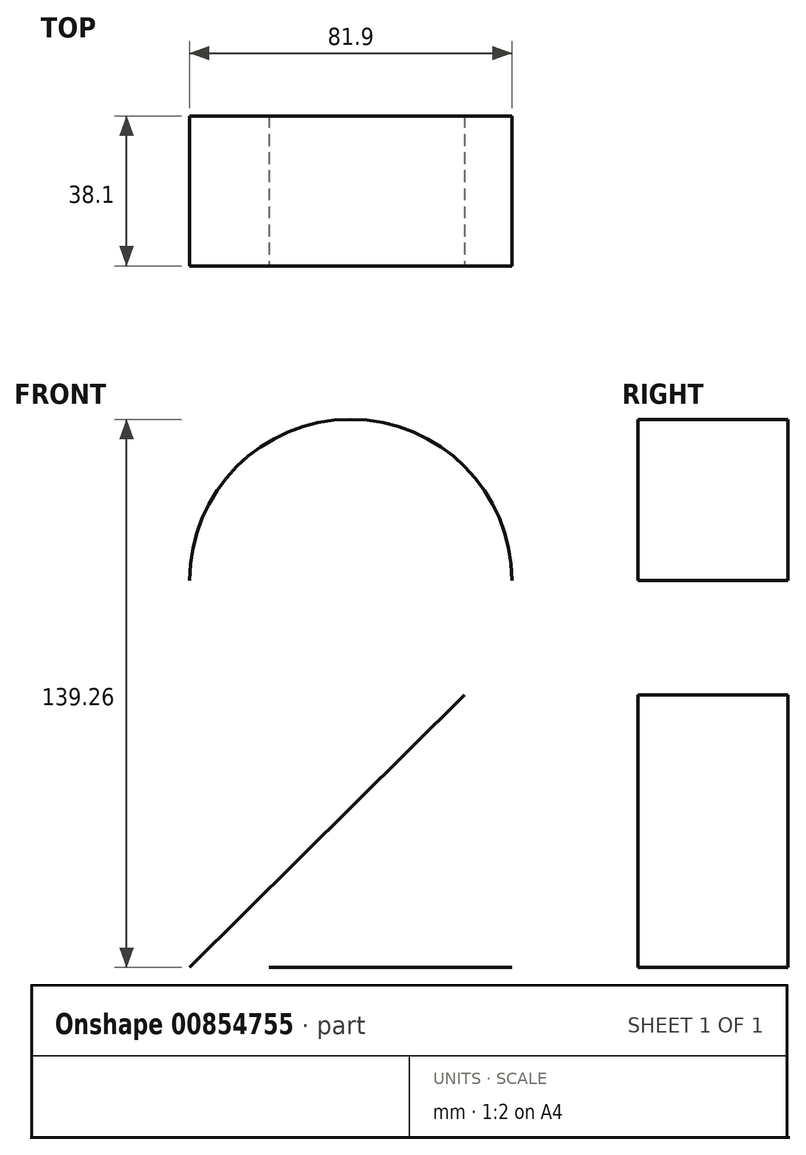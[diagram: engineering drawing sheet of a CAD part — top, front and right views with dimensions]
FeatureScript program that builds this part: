
annotation { "Feature Type Name" : "Feature", "Feature Type Description" : "" }
export const myFeature = defineFeature(function(context is Context, id is Id, definition is map)
    precondition{}
    {
        {
            var Q0;
            Q0=qCreatedBy(makeId("Front.planeOp"),FACE);
            var sketch = newSketch(context, id + "F0", { "sketchPlane" : qUnion([Q0])});
            skArc(sketch, "E0", {"start": v(40.95, 0) * mm, "mid": v(0, 40.95) * mm, "end": v(-40.95, 0) * mm});
            skLineSegment(sketch, "E1", {"start": v(28.84, -29.07) * mm, "end": v(-40.95, -98.31) * mm});
            skLineSegment(sketch, "E2", {"start": v(-20.82, -98.31) * mm, "end": v(40.95, -98.31) * mm});
            skLineSegment(sketch, "E3", {"start": v(-55.83, 0) * mm, "end": v(53.18, 0) * mm, "construction": true});
            skLineSegment(sketch, "E4", {"start": v(-20.82, -98.31) * mm, "end": v(-20.82, -130.32) * mm, "construction": true});
            skSolve(sketch);
        }
        {
            var Q0;
            Q0 = qSketchRegion(id + "F0", true);
            var Q1;
            Q1 = qBodyType(qCreatedBy(id + "F0" ,EDGE), BodyType.WIRE);
            extrude(context, id + "F1", {"entities" : qUnion([Q0]), "bodyType" : ToolBodyType.SURFACE, "surfaceEntities" : qUnion([Q1]), "depth" : 38.1 * mm, "offsetDistance" : 25.4 * mm});
        }
    });
